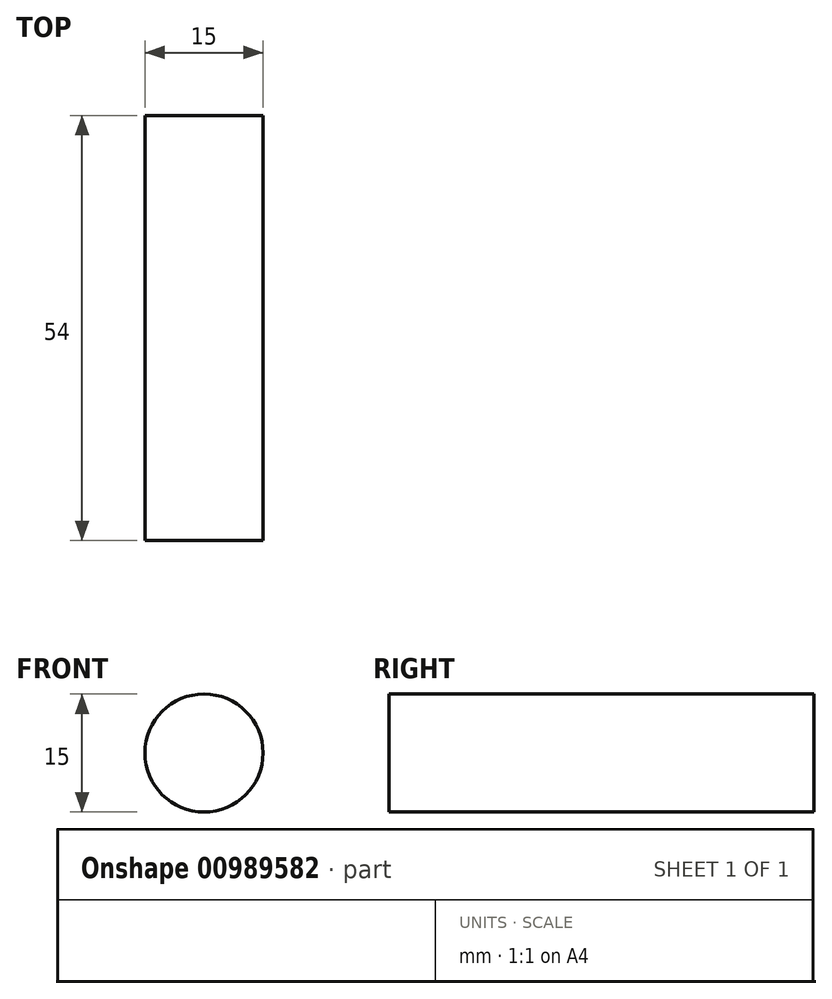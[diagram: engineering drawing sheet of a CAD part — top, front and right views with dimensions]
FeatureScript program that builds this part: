
annotation { "Feature Type Name" : "Feature", "Feature Type Description" : "" }
export const myFeature = defineFeature(function(context is Context, id is Id, definition is map)
    precondition{}
    {
        {
            var Q0;
            Q0=qCreatedBy(makeId("Front.planeOp"),FACE);
            var sketch = newSketch(context, id + "F0", { "sketchPlane" : qUnion([Q0])});
            skCircle(sketch, "E0", {"center": v(0, 0) * mm, "radius": 7.5 * mm});
            skSolve(sketch);
        }
        {
            var Q0;
            Q0 = qSketchRegion(id + "F0", true);
            extrude(context, id + "F1", {"entities" : qUnion([Q0]), "oppositeDirection" : true, "depth" : 54 * mm, "offsetDistance" : 25 * mm});
        }
    });
